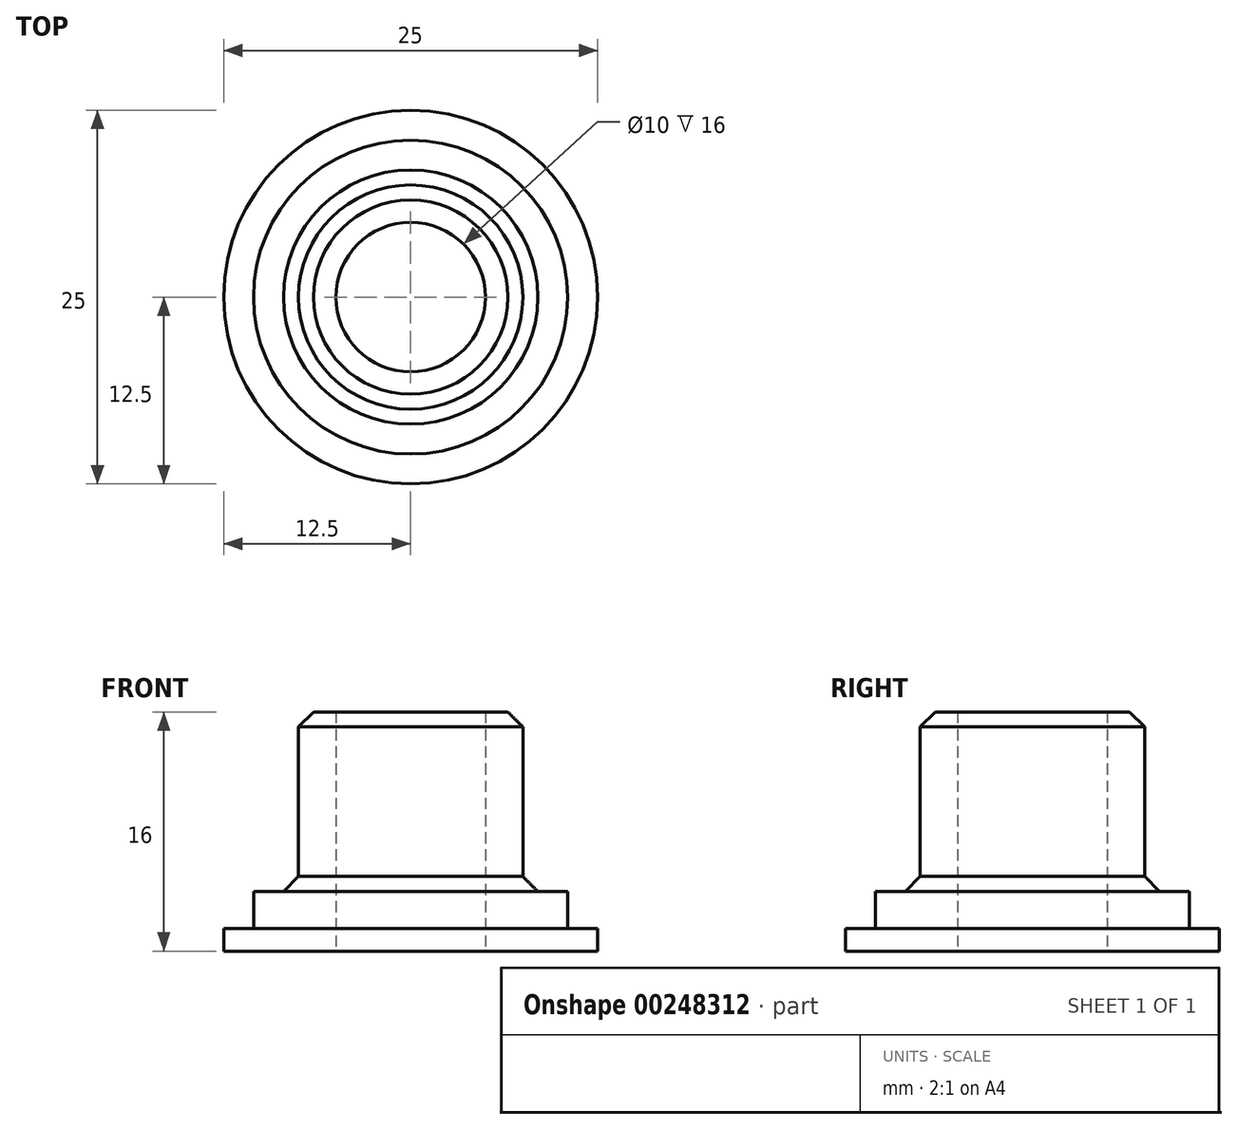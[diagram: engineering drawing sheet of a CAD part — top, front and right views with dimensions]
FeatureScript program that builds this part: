
annotation { "Feature Type Name" : "Feature", "Feature Type Description" : "" }
export const myFeature = defineFeature(function(context is Context, id is Id, definition is map)
    precondition{}
    {
        {
            var Q0;
            Q0=qCreatedBy(makeId("Top.planeOp"),FACE);
            var sketch = newSketch(context, id + "F0", { "sketchPlane" : qUnion([Q0])});
            skCircle(sketch, "E0", {"center": v(0, 0) * mm, "radius": 5 * mm});
            skCircle(sketch, "E1", {"center": v(0, 0) * mm, "radius": 10.5 * mm});
            skCircle(sketch, "E2", {"center": v(0, 0) * mm, "radius": 12.5 * mm});
            skCircle(sketch, "E3", {"center": v(0, 0) * mm, "radius": 7.5 * mm});
            skSolve(sketch);
        }
        {
            var Q0;
            Q0=makeQuery(id+"F0.imprint","IMPRINT",FACE,{"disambiguationData":[TD([[makeQuery(id+"F0.imprint","IMPRINT",EDGE,{"derivedFrom":sQuery(id+"F0.wireOp",EDGE,"E0")}),-1.0]])]});
            var Q1;
            Q1=makeQuery(id+"F0.imprint","IMPRINT",FACE,{"disambiguationData":[TD([[makeQuery(id+"F0.imprint","IMPRINT",EDGE,{"derivedFrom":sQuery(id+"F0.wireOp",EDGE,"E1")}),-1.0]])]});
            var Q2;
            Q2=makeQuery(id+"F0.imprint","IMPRINT",FACE,{"disambiguationData":[TD([[makeQuery(id+"F0.imprint","IMPRINT",EDGE,{"derivedFrom":sQuery(id+"F0.wireOp",EDGE,"E1")}),1.0]])]});
            extrude(context, id + "F1", {"entities" : qUnion([Q0, Q1, Q2]), "depth" : 1.5 * mm});
        }
        {
            var Q0;
            Q0=makeQuery(id+"F0.imprint","IMPRINT",FACE,{"disambiguationData":[TD([[makeQuery(id+"F0.imprint","IMPRINT",EDGE,{"derivedFrom":sQuery(id+"F0.wireOp",EDGE,"E0")}),-1.0]])]});
            var Q1;
            Q1=makeQuery(id+"F0.imprint","IMPRINT",FACE,{"disambiguationData":[TD([[makeQuery(id+"F0.imprint","IMPRINT",EDGE,{"derivedFrom":sQuery(id+"F0.wireOp",EDGE,"E1")}),1.0]])]});
            extrude(context, id + "F2", {"entities" : qUnion([Q0, Q1]), "operationType" : NewBodyOperationType.ADD, "depth" : 4 * mm});
        }
        {
            var Q0;
            Q0=makeQuery(id+"F0.imprint","IMPRINT",FACE,{"disambiguationData":[TD([[makeQuery(id+"F0.imprint","IMPRINT",EDGE,{"derivedFrom":sQuery(id+"F0.wireOp",EDGE,"E0")}),-1.0]])]});
            extrude(context, id + "F3", {"entities" : qUnion([Q0]), "operationType" : NewBodyOperationType.ADD, "depth" : 16 * mm});
        }
        {
            var Q0;
            Q0=makeQuery(id+"F3.opExtrude","CAP_EDGE",EDGE,{"disambiguationData":[OSD([sQuery(id+"F0.wireOp",EDGE,"E3")])],"isStart":false});
            var Q1;
            Q1=makeQuery(id+"F3.boolean.opBoolean","INTERSECT",EDGE,{"derivedFrom":[makeQuery(id+"F2.opExtrude","CAP_FACE",FACE,{"disambiguationData":[OSD([sQuery(id+"F0.wireOp",EDGE,"E0"),sQuery(id+"F0.wireOp",EDGE,"E1")])],"isStart":false}),makeQuery(id+"F3.opExtrude","SWEPT_FACE",FACE,{"disambiguationData":[OSD([sQuery(id+"F0.wireOp",EDGE,"E3")])]})]});
            chamfer(context, id + "F4", {"entities" : qUnion([Q0, Q1]), "width" : 1 * mm, "tangentPropagation" : true});
        }
    });
